# Revit family: 28_CC_MOD_kolom_hout
name_source: partatom
category: Structural Columns
revit_build: Autodesk Revit Architecture 2012
units: mm (PartAtom-declared; Revit-internal decimal feet)

## types (24) — shared parameters

## per-type parameters (varying)
| type | A | Ix | Iy | Sx | Sy | breedte | dikte |
| 38x64 | 0 m² | 19.844 | 7.14 | 419.6 | 15.36 | 38 mm | 64 mm |
| 38x89 | 0 m² | 54.451 | 10 | 822.4 | 21.51 | 38 mm | 89 mm |
| 38x114 | 0 m² | 115.73 | 12.86 | 1359 | 27.65 | 38 mm | 114 mm |
| 38x140 | 0.01 m² | 211.3 | 15.72 | 2031 | 33.8 | 38 mm | 140 mm |
| 38x184 | 0.01 m² | 483.97 | 20.72 | 3529 | 44.55 | 38 mm | 184 mm |
| 38x235 | 0.01 m² | 1005.15 | 26.43 | 5744 | 56.84 | 38 mm | 235 mm |
| 38x286 | 0.01 m² | 1808.3 | 32.15 | 8497 | 69.13 | 38 mm | 286 mm |
| 38x337 | 0.01 m² | 2954.3 | 37.86 | 11786 | 81.42 | 38 mm | 337 mm |
| 64x89 | 0.01 m² | 90.752 | 46.3 | 1371 | 59.74 | 64 mm | 89 mm |
| 64x114 | 0.01 m² | 192.88 | 59.53 | 2266 | 76.81 | 64 mm | 114 mm |
| 64x140 | 0.01 m² | 352.16 | 72.76 | 3385 | 93.88 | 64 mm | 140 mm |
| 64x184 | 0.01 m² | 806.62 | 95.91 | 5881 | 123.8 | 64 mm | 184 mm |
| 64x235 | 0.01 m² | 1675.2 | 122.4 | 9574 | 157.9 | 64 mm | 235 mm |
| 64x286 | 0.02 m² | 3013.8 | 148.8 | 14161 | 192 | 64 mm | 286 mm |
| 64x337 | 0.02 m² | 4923.8 | 175.3 | 19644 | 226 | 64 mm | 337 mm |
| 64x387 | 0.02 m² | 7506.9 | 201.7 | 26021 | 260 | 64 mm | 387 mm |
| 89x89 | 0.01 m² | 127.05 | 127.1 | 1919 | 117 | 89 mm | 89 mm |
| 89x114 | 0.01 m² | 270.03 | 163.4 | 3172 | 151 | 89 mm | 114 mm |
| 89x140 | 0.01 m² | 493.02 | 199.7 | 4739 | 184 | 89 mm | 140 mm |
| 89x184 | 0.02 m² | 1129.3 | 263.2 | 8234 | 243 | 89 mm | 184 mm |
| 89x235 | 0.02 m² | 2345.3 | 335.8 | 13403 | 309 | 89 mm | 235 mm |
| 89x286 | 0.03 m² | 4219.3 | 408.4 | 19825 | 376 | 89 mm | 286 mm |
| 89x337 | 0.03 m² | 7290.9 | 490.1 | 28549 | 452 | 89 mm | 343 mm |
| 89x387 | 0.04 m² | 11035 | 562.7 | 37634 | 519 | 89 mm | 394 mm |

## geometry (parser evidence)
native form markers: Sweep x1
no freeform markers — native parametric forms only
